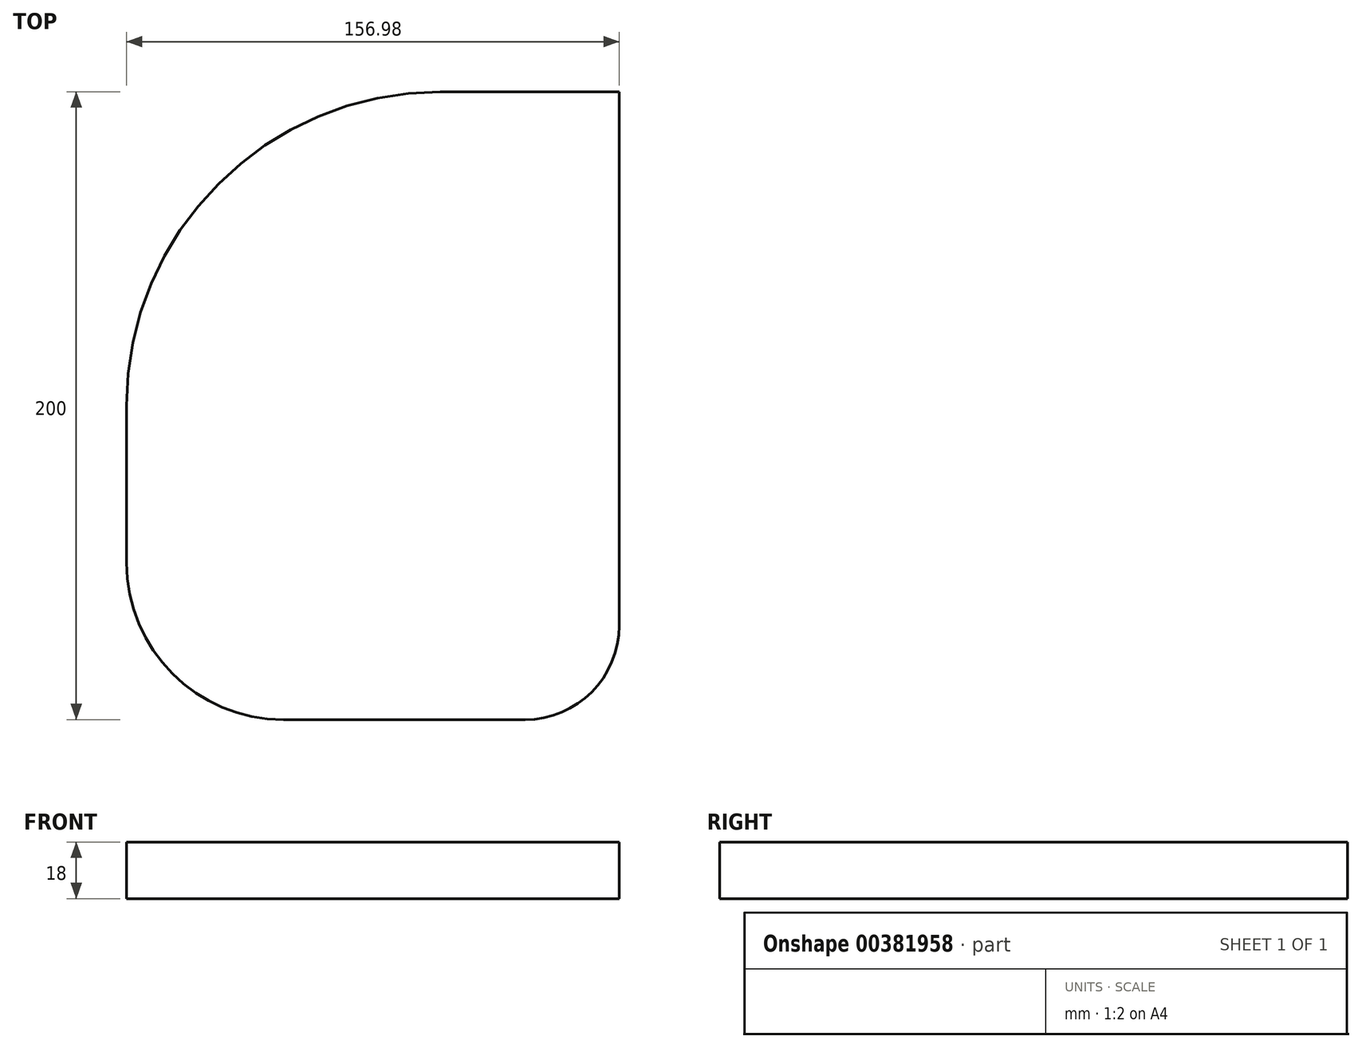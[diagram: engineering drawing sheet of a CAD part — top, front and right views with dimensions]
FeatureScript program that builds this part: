
annotation { "Feature Type Name" : "Feature", "Feature Type Description" : "" }
export const myFeature = defineFeature(function(context is Context, id is Id, definition is map)
    precondition{}
    {
        {
            var Q0;
            Q0=qCreatedBy(makeId("Top.planeOp"),FACE);
            var sketch = newSketch(context, id + "F0", { "sketchPlane" : qUnion([Q0])});
            skLineSegment(sketch, "E0.bottom", {"start": v(48.49, -100) * mm, "end": v(-28.49, -100) * mm});
            skLineSegment(sketch, "E0.top", {"start": v(78.49, 100) * mm, "end": v(21.51, 100) * mm});
            skLineSegment(sketch, "E0.left", {"start": v(78.49, -70) * mm, "end": v(78.49, 100) * mm});
            skLineSegment(sketch, "E0.right", {"start": v(-78.49, -50) * mm, "end": v(-78.49, 0) * mm});
            skPoint(sketch, "E0.middle", {"position": v(0, 0) * mm});
            skPoint(sketch, "E1.visualSharp", {"position": v(-78.49, 100) * mm});
            skArc(sketch, "E1.filletArc", {"start": v(21.51, 100) * mm, "mid": v(-49.2, 70.71) * mm, "end": v(-78.49, 0) * mm});
            skPoint(sketch, "E2.visualSharp", {"position": v(-78.49, -100) * mm});
            skArc(sketch, "E2.filletArc", {"start": v(-78.49, -50) * mm, "mid": v(-63.84, -85.36) * mm, "end": v(-28.49, -100) * mm});
            skPoint(sketch, "E3.visualSharp", {"position": v(78.49, -100) * mm});
            skArc(sketch, "E3.filletArc", {"start": v(48.49, -100) * mm, "mid": v(69.7, -91.21) * mm, "end": v(78.49, -70) * mm});
            skSolve(sketch);
        }
        {
            var Q0;
            Q0=makeQuery(id+"F0.imprint","IMPRINT",FACE,{"disambiguationData":[TD([[makeQuery(id+"F0.imprint","IMPRINT",EDGE,{"derivedFrom":sQuery(id+"F0.wireOp",EDGE,"E0.bottom")}),-1.0]])]});
            var Q1;
            Q1=sQuery(id+"F0.wireOp",EDGE,"E1.filletArc");
            var Q2;
            Q2=sQuery(id+"F0.wireOp",EDGE,"E0.right");
            extrude(context, id + "F1", {"entities" : qUnion([Q0]), "surfaceEntities" : qUnion([Q1, Q2]), "depth" : 18 * mm});
        }
    });
